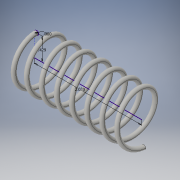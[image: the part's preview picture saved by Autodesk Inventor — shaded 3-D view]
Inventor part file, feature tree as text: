
AUTODESK INVENTOR PART (.ipt)
format: ipt  version: 2016 (Build 200138000, 138)  size: 386,560 bytes
history: native  units: in
note: dims shown in document units (in); Inventor stores cm internally (conversion verified against a paired STEP export)
features: helix x1, sketch x1
ambient origin geometry x8: Origin, YZ Plane, XZ Plane, XY Plane, X Axis, Y Axis, Z Axis, Center Point
bodies: Solid1 (feature_tree)
feature tree (2):
  helix  "Coil1"  [1 undecoded]
  sketch  "Sketch1"  dims[d1=0.08in d2=0.429in d3=1.0in d4=2.03in d5=2.7559in d6=0.0in d7=90.0deg d8=90.0deg d9=0.0in d10=0.0in]
note: 1 required parameter value undecoded (feature->parameter linkage not recoverable at this tier; creation-order binding heuristic only, values carry confidence <= 0.55)
